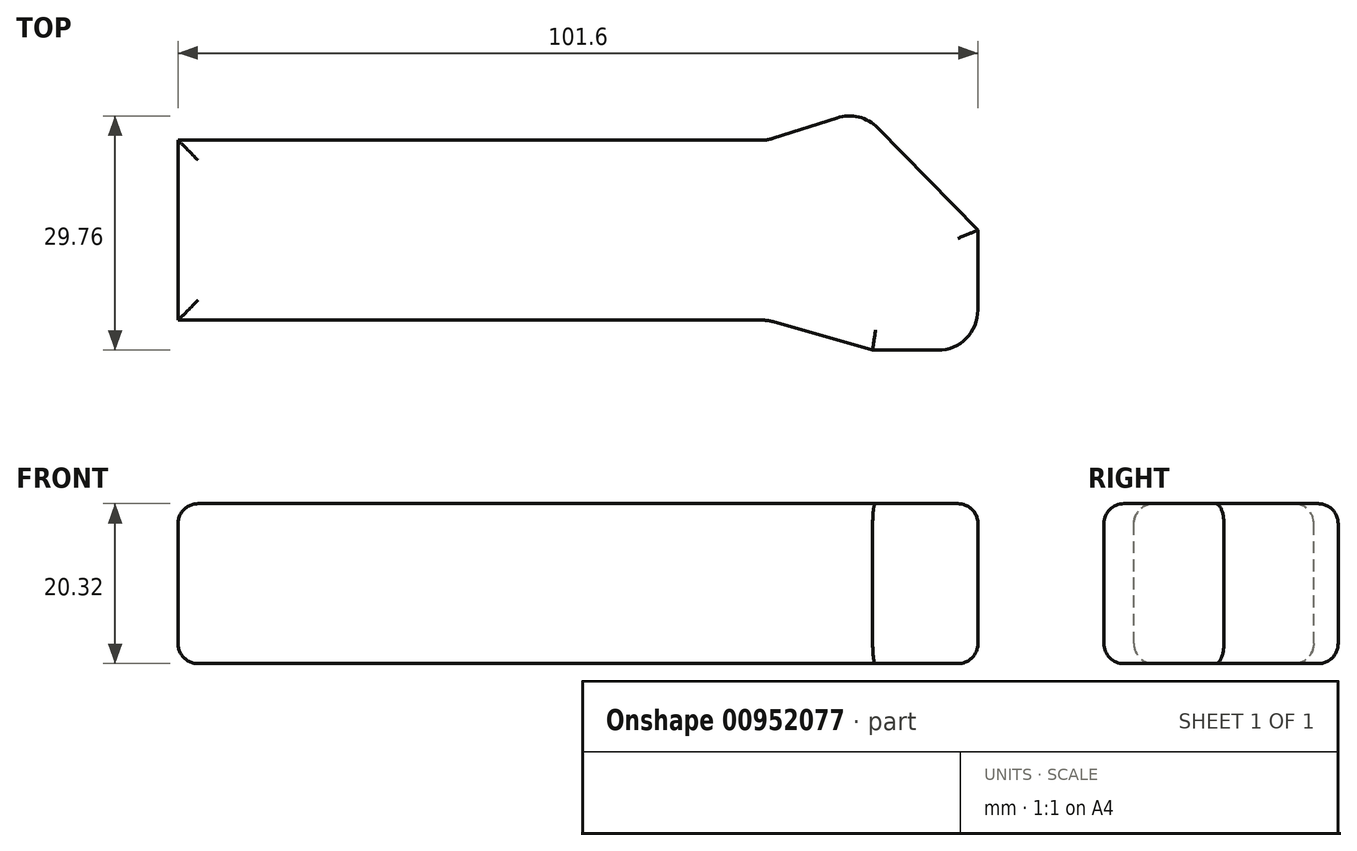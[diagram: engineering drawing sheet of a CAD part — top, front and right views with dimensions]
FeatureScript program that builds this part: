
annotation { "Feature Type Name" : "Feature", "Feature Type Description" : "" }
export const myFeature = defineFeature(function(context is Context, id is Id, definition is map)
    precondition{}
    {
        {
            var Q0;
            Q0=qCreatedBy(makeId("Top.planeOp"),FACE);
            var sketch = newSketch(context, id + "F0", { "sketchPlane" : qUnion([Q0])});
            skLineSegment(sketch, "E0.bottom", {"start": v(50.8, -15.24) * mm, "end": v(-50.8, -15.24) * mm});
            skLineSegment(sketch, "E0.top", {"start": v(50.8, 15.24) * mm, "end": v(-50.8, 15.24) * mm});
            skLineSegment(sketch, "E0.left", {"start": v(50.8, -15.24) * mm, "end": v(50.8, 15.24) * mm});
            skLineSegment(sketch, "E0.right", {"start": v(-50.8, -15.24) * mm, "end": v(-50.8, 15.24) * mm});
            skPoint(sketch, "E0.middle", {"position": v(0, 0) * mm});
            skSolve(sketch);
        }
        {
            var Q0;
            Q0 = qSketchRegion(id + "F0", true);
            extrude(context, id + "F1", {"entities" : qUnion([Q0]), "depth" : 10.16 * mm, "offsetDistance" : 25.4 * mm, "hasSecondDirection" : true, "secondDirectionOppositeDirection" : true, "secondDirectionDepth" : 10.16 * mm});
        }
        {
            var Q0;
            Q0=makeQuery(id+"F1.opExtrude","CAP_FACE",FACE,{"disambiguationData":[OSD([sQuery(id+"F0.wireOp",EDGE,"E0.bottom"),sQuery(id+"F0.wireOp",EDGE,"E0.top"),sQuery(id+"F0.wireOp",EDGE,"E0.left"),sQuery(id+"F0.wireOp",EDGE,"E0.right")])],"isStart":false});
            var sketch = newSketch(context, id + "F2", { "sketchPlane" : qUnion([Q0])});
            skLineSegment(sketch, "E1", {"start": v(24.06, -11.43) * mm, "end": v(-50.8, -11.43) * mm});
            skLineSegment(sketch, "E2", {"start": v(-50.8, -11.43) * mm, "end": v(-50.8, 11.43) * mm});
            skLineSegment(sketch, "E3", {"start": v(-50.8, 11.43) * mm, "end": v(24.06, 11.43) * mm});
            skLineSegment(sketch, "E4", {"start": v(24.06, 11.43) * mm, "end": v(35.88, 15.24) * mm});
            skLineSegment(sketch, "E5", {"start": v(35.88, 15.24) * mm, "end": v(50.8, 0) * mm});
            skLineSegment(sketch, "E6", {"start": v(50.8, 0) * mm, "end": v(50.8, -15.24) * mm});
            skLineSegment(sketch, "E7", {"start": v(37.43, -15.24) * mm, "end": v(24.06, -11.43) * mm});
            skPoint(sketch, "E7.startSnap0", {"position": v(37.43, -13.33) * mm});
            skLineSegment(sketch, "E8", {"start": v(37.43, -15.24) * mm, "end": v(50.8, -15.24) * mm});
            skLineSegment(sketch, "E9", {"start": v(50.8, 0) * mm, "end": v(61.73, 0) * mm});
            skLineSegment(sketch, "E10", {"start": v(61.73, 0) * mm, "end": v(61.73, 22.96) * mm});
            skLineSegment(sketch, "E11", {"start": v(61.73, 22.96) * mm, "end": v(-64.56, 22.96) * mm});
            skLineSegment(sketch, "E12", {"start": v(-64.56, 22.96) * mm, "end": v(-64.56, -22.59) * mm});
            skLineSegment(sketch, "E13", {"start": v(-64.56, -22.59) * mm, "end": v(63.7, -22.59) * mm});
            skLineSegment(sketch, "E14", {"start": v(63.7, -22.59) * mm, "end": v(50.8, -15.24) * mm});
            skSolve(sketch);
        }
        {
            var Q0;
            {var subQ0=sQuery(id+"F2.wireOp",EDGE,"E1");Q0=makeQuery(id+"F2.imprint","IMPRINT",FACE,{"disambiguationData":[TD([[makeQuery(id+"F2.imprint","IMPRINT",EDGE,{"derivedFrom":subQ0}),1.0]])]});}
            var Q1;
            {var subQ0=sQuery(id+"F2.wireOp",EDGE,"E5");Q1=makeQuery(id+"F2.imprint","IMPRINT",FACE,{"disambiguationData":[TD([[makeQuery(id+"F2.imprint","IMPRINT",EDGE,{"derivedFrom":subQ0}),1.0]])]});}
            var Q2;
            {var subQ0=sQuery(id+"F2.wireOp",EDGE,"E3");Q2=makeQuery(id+"F2.imprint","IMPRINT",FACE,{"disambiguationData":[TD([[makeQuery(id+"F2.imprint","IMPRINT",EDGE,{"derivedFrom":subQ0}),1.0]])]});}
            var Q3;
            {var subQ9=sQuery(id+"F2.wireOp",EDGE,"E2");Q3=makeQuery(id+"F2.imprint","IMPRINT",FACE,{"disambiguationData":[TD([[makeQuery(id+"F2.imprint","IMPRINT",EDGE,{"derivedFrom":subQ9}),1.0]])]});}
            extrude(context, id + "F3", {"entities" : qUnion([Q0, Q1, Q2, Q3]), "operationType" : NewBodyOperationType.REMOVE, "oppositeDirection" : true, "depth" : 25.4 * mm, "offsetDistance" : 25.4 * mm});
        }
        {
            var Q0;
            Q0=makeQuery(id+"F3.boolean.opBoolean","COPY",EDGE,{"derivedFrom":makeQuery(id+"F3.opExtrude","SWEPT_EDGE",EDGE,{"disambiguationData":[OSD([sQuery(id+"F0.wireOp",EDGE,"E0.top"),sQuery(id+"F2.wireOp",EDGE,"E4"),sQuery(id+"F2.wireOp",EDGE,"E5")])]})});
            var Q1;
            Q1=makeQuery(id+"F3.boolean.opBoolean","COPY",EDGE,{"derivedFrom":makeQuery(id+"F3.opExtrude","SWEPT_EDGE",EDGE,{"disambiguationData":[OSD([sQuery(id+"F2.wireOp",EDGE,"E3"),sQuery(id+"F2.wireOp",EDGE,"E4")])]})});
            var Q2;
            Q2=makeQuery(id+"F1.opExtrude","SWEPT_EDGE",EDGE,{"disambiguationData":[OSD([sQuery(id+"F0.wireOp",EDGE,"E0.bottom"),sQuery(id+"F0.wireOp",EDGE,"E0.left")])]});
            var Q3;
            Q3=makeQuery(id+"F3.boolean.opBoolean","COPY",EDGE,{"derivedFrom":makeQuery(id+"F3.opExtrude","SWEPT_EDGE",EDGE,{"disambiguationData":[OSD([sQuery(id+"F0.wireOp",EDGE,"E0.bottom"),sQuery(id+"F2.wireOp",EDGE,"E7"),sQuery(id+"F2.wireOp",EDGE,"E8")])]})});
            var Q4;
            Q4=makeQuery(id+"F3.boolean.opBoolean","COPY",EDGE,{"derivedFrom":makeQuery(id+"F3.opExtrude","SWEPT_EDGE",EDGE,{"disambiguationData":[OSD([sQuery(id+"F2.wireOp",EDGE,"E1"),sQuery(id+"F2.wireOp",EDGE,"E7")])]})});
            var Q5;
            Q5=makeQuery(id+"F3.boolean.opBoolean","COPY",EDGE,{"derivedFrom":makeQuery(id+"F3.opExtrude","SWEPT_EDGE",EDGE,{"disambiguationData":[OSD([sQuery(id+"F0.wireOp",EDGE,"E0.right"),sQuery(id+"F2.wireOp",EDGE,"E1"),sQuery(id+"F2.wireOp",EDGE,"E2")])]})});
            var Q6;
            Q6=makeQuery(id+"F3.boolean.opBoolean","COPY",EDGE,{"derivedFrom":makeQuery(id+"F3.opExtrude","SWEPT_EDGE",EDGE,{"disambiguationData":[OSD([sQuery(id+"F0.wireOp",EDGE,"E0.right"),sQuery(id+"F2.wireOp",EDGE,"E2"),sQuery(id+"F2.wireOp",EDGE,"E3")])]})});
            var Q7;
            Q7=makeQuery(id+"F3.boolean.opBoolean","COPY",EDGE,{"derivedFrom":makeQuery(id+"F3.opExtrude","SWEPT_EDGE",EDGE,{"disambiguationData":[OSD([sQuery(id+"F0.wireOp",EDGE,"E0.left"),sQuery(id+"F2.wireOp",EDGE,"E5"),sQuery(id+"F2.wireOp",EDGE,"E6"),sQuery(id+"F2.wireOp",EDGE,"E9")])]})});
            fillet(context, id + "F4", {"entities" : qUnion([Q0, Q1, Q2, Q3, Q4, Q5, Q6, Q7]), "radius" : 5.08 * mm, "tangentPropagation" : true, "allowEdgeOverflow" : false});
        }
        {
            var Q0;
            Q0=makeQuery(id+"F1.opExtrude","CAP_FACE",FACE,{"disambiguationData":[OSD([sQuery(id+"F0.wireOp",EDGE,"E0.bottom"),sQuery(id+"F0.wireOp",EDGE,"E0.top"),sQuery(id+"F0.wireOp",EDGE,"E0.left"),sQuery(id+"F0.wireOp",EDGE,"E0.right")])],"isStart":true});
            var Q1;
            Q1=makeQuery(id+"F1.opExtrude","CAP_FACE",FACE,{"disambiguationData":[OSD([sQuery(id+"F0.wireOp",EDGE,"E0.bottom"),sQuery(id+"F0.wireOp",EDGE,"E0.top"),sQuery(id+"F0.wireOp",EDGE,"E0.left"),sQuery(id+"F0.wireOp",EDGE,"E0.right")])],"isStart":false});
            fillet(context, id + "F5", {"entities" : qUnion([Q0, Q1]), "radius" : 2.54 * mm, "tangentPropagation" : true, "allowEdgeOverflow" : false});
        }
    });
